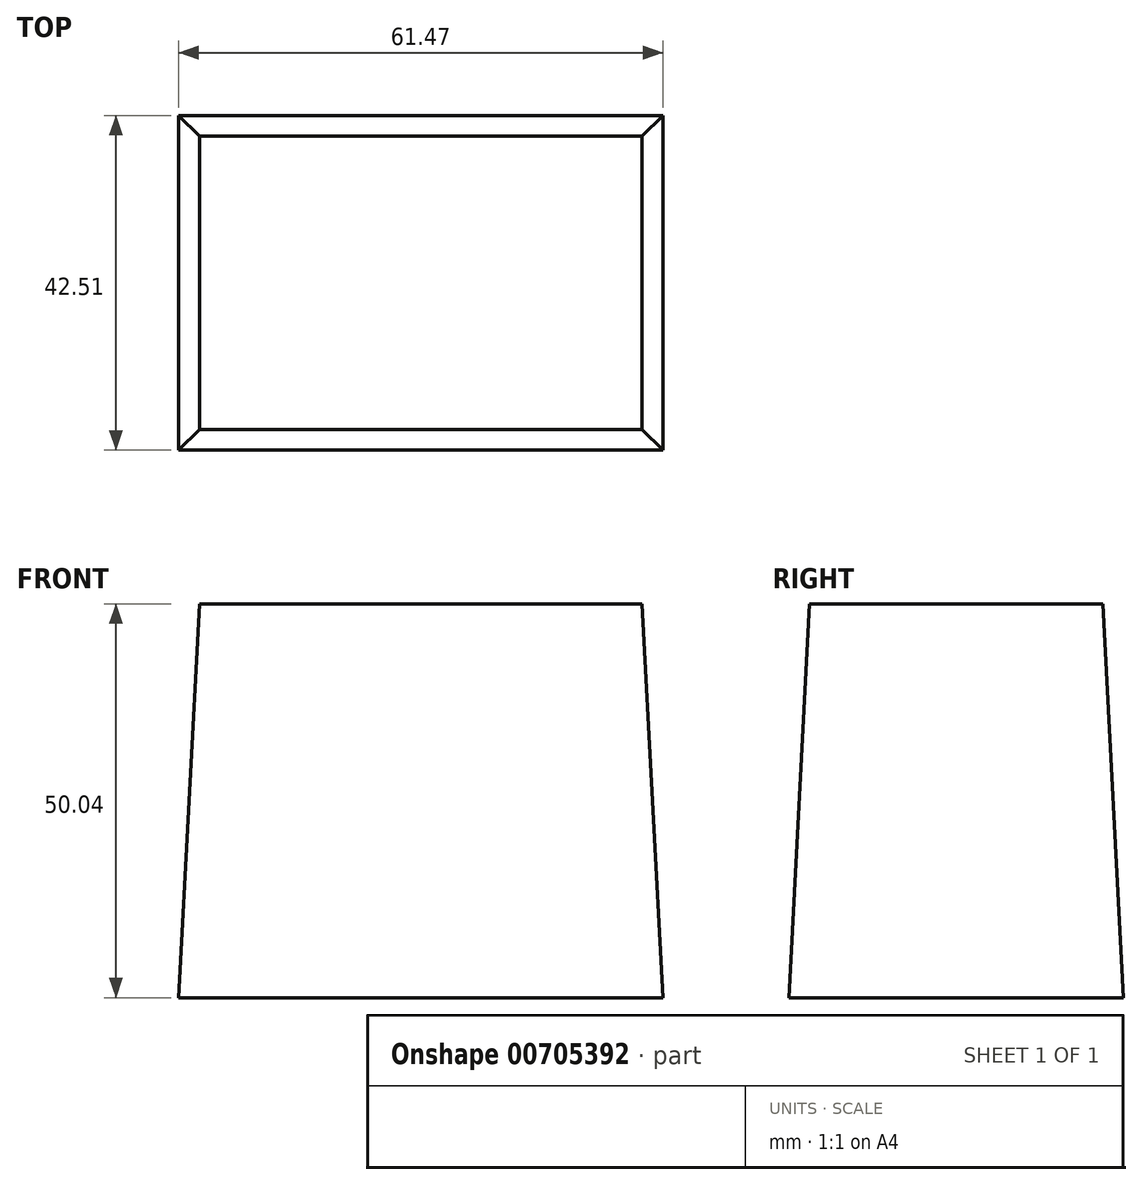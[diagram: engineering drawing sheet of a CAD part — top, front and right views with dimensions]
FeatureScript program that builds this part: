
annotation { "Feature Type Name" : "Feature", "Feature Type Description" : "" }
export const myFeature = defineFeature(function(context is Context, id is Id, definition is map)
    precondition{}
    {
        {
            var Q0;
            Q0=qCreatedBy(makeId("Top.planeOp"),FACE);
            var sketch = newSketch(context, id + "F0", { "sketchPlane" : qUnion([Q0])});
            skLineSegment(sketch, "E0.bottom", {"start": v(0, 0) * mm, "end": v(61.47, 0) * mm});
            skLineSegment(sketch, "E0.top", {"start": v(0, 42.51) * mm, "end": v(61.47, 42.51) * mm});
            skLineSegment(sketch, "E0.left", {"start": v(0, 0) * mm, "end": v(0, 42.51) * mm});
            skLineSegment(sketch, "E0.right", {"start": v(61.47, 0) * mm, "end": v(61.47, 42.51) * mm});
            skSolve(sketch);
        }
        {
            var Q0;
            Q0=makeQuery(id+"F0.imprint","IMPRINT",FACE,{"disambiguationData":[TD([[makeQuery(id+"F0.imprint","IMPRINT",EDGE,{"derivedFrom":sQuery(id+"F0.wireOp",EDGE,"E0.bottom")}),1.0]])]});
            extrude(context, id + "F1", {"entities" : qUnion([Q0]), "depth" : 50.04 * mm, "offsetDistance" : 25.4 * mm, "hasDraft" : true, "draftAngle" : 3 * degree, "draftPullDirection" : true});
        }
    });
